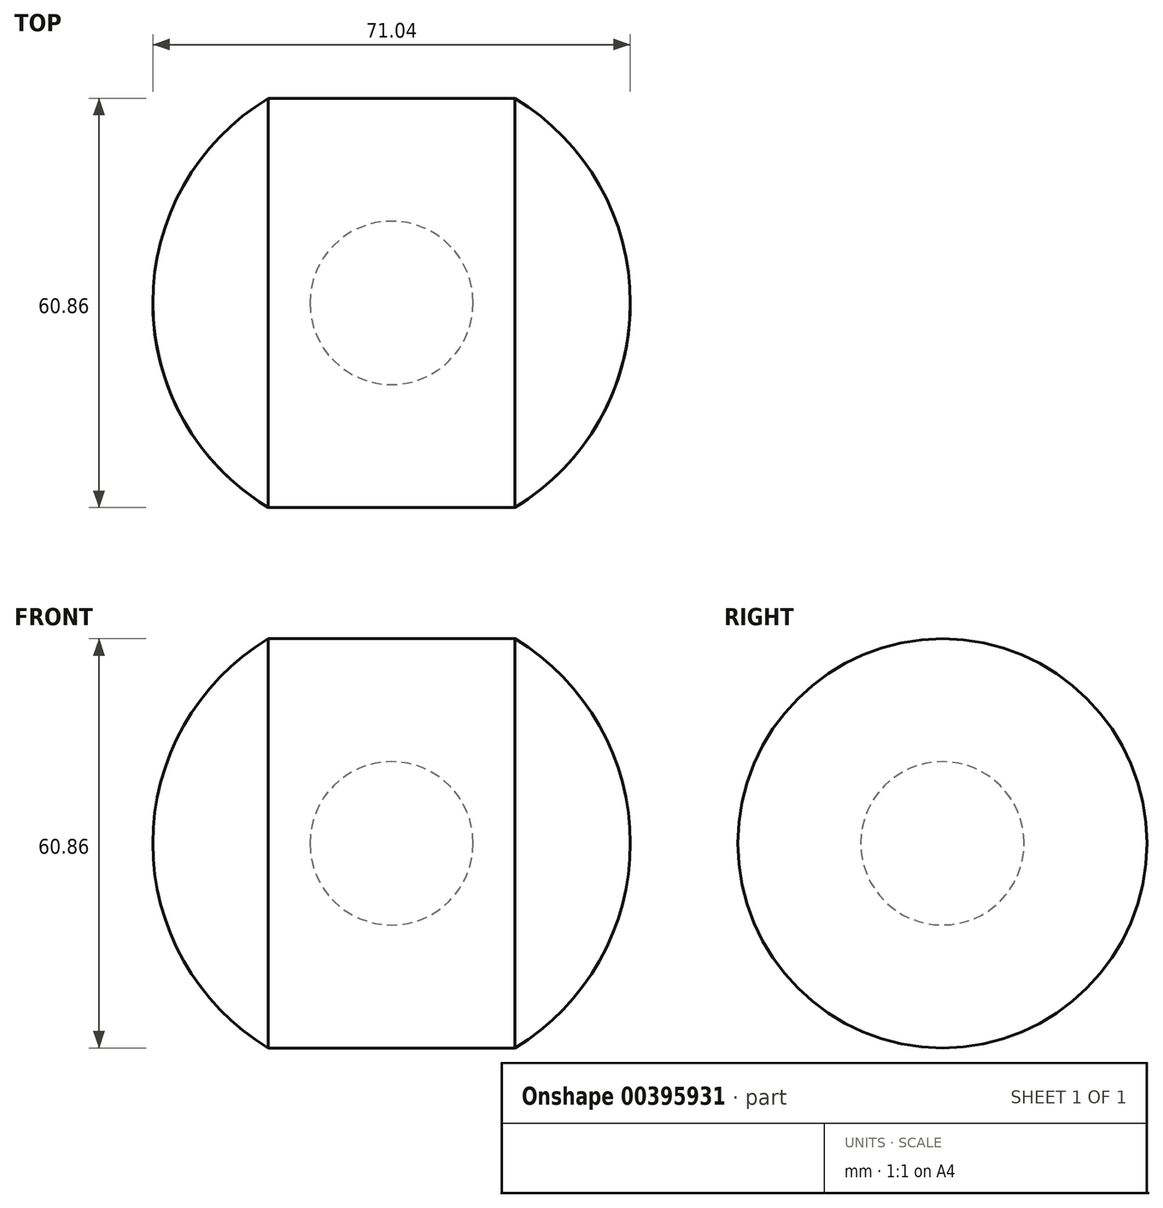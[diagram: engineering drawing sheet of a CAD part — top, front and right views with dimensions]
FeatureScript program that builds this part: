
annotation { "Feature Type Name" : "Feature", "Feature Type Description" : "" }
export const myFeature = defineFeature(function(context is Context, id is Id, definition is map)
    precondition{}
    {
        {
            var Q0;
            Q0=qCreatedBy(makeId("Top.planeOp"),FACE);
            var sketch = newSketch(context, id + "F0", { "sketchPlane" : qUnion([Q0])});
            skCircle(sketch, "E0", {"center": v(0, 0) * mm, "radius": 35.52 * mm});
            skLineSegment(sketch, "E1", {"start": v(-35.52, 0) * mm, "end": v(35.52, 0) * mm});
            skLineSegment(sketch, "E2.bottom", {"start": v(-18.34, -30.43) * mm, "end": v(18.9, -30.43) * mm});
            skLineSegment(sketch, "E2.top", {"start": v(-18.34, -51.23) * mm, "end": v(18.9, -51.23) * mm});
            skLineSegment(sketch, "E2.left", {"start": v(-18.34, -30.43) * mm, "end": v(-18.34, -51.23) * mm});
            skLineSegment(sketch, "E2.right", {"start": v(18.9, -30.43) * mm, "end": v(18.9, -51.23) * mm});
            skLineSegment(sketch, "E3.left", {"start": v(-34.7, 7.64) * mm, "end": v(-34.7, -6.82) * mm});
            skCircle(sketch, "E4", {"center": v(0, 0) * mm, "radius": 12.15 * mm});
            skSolve(sketch);
        }
        {
            var Q0;
            {var subQ0=sQuery(id+"F0.wireOp",EDGE,"E1");Q0=makeQuery(id+"F0.imprint","IMPRINT",FACE,{"disambiguationData":[TD([[makeQuery(id+"F0.imprint","IMPRINT",EDGE,{"derivedFrom":subQ0}),-1.0]])]});}
            var Q1;
            Q1=sQuery(id+"F0.wireOp",EDGE,"E0");
            var Q2;
            Q2=sQuery(id+"F0.wireOp",EDGE,"E1");
            revolve(context, id + "F1", {"entities" : qUnion([Q0]), "surfaceEntities" : qUnion([Q1]), "axis" : qUnion([Q2]), "revolveType" : RevolveType.FULL});
        }
    });
